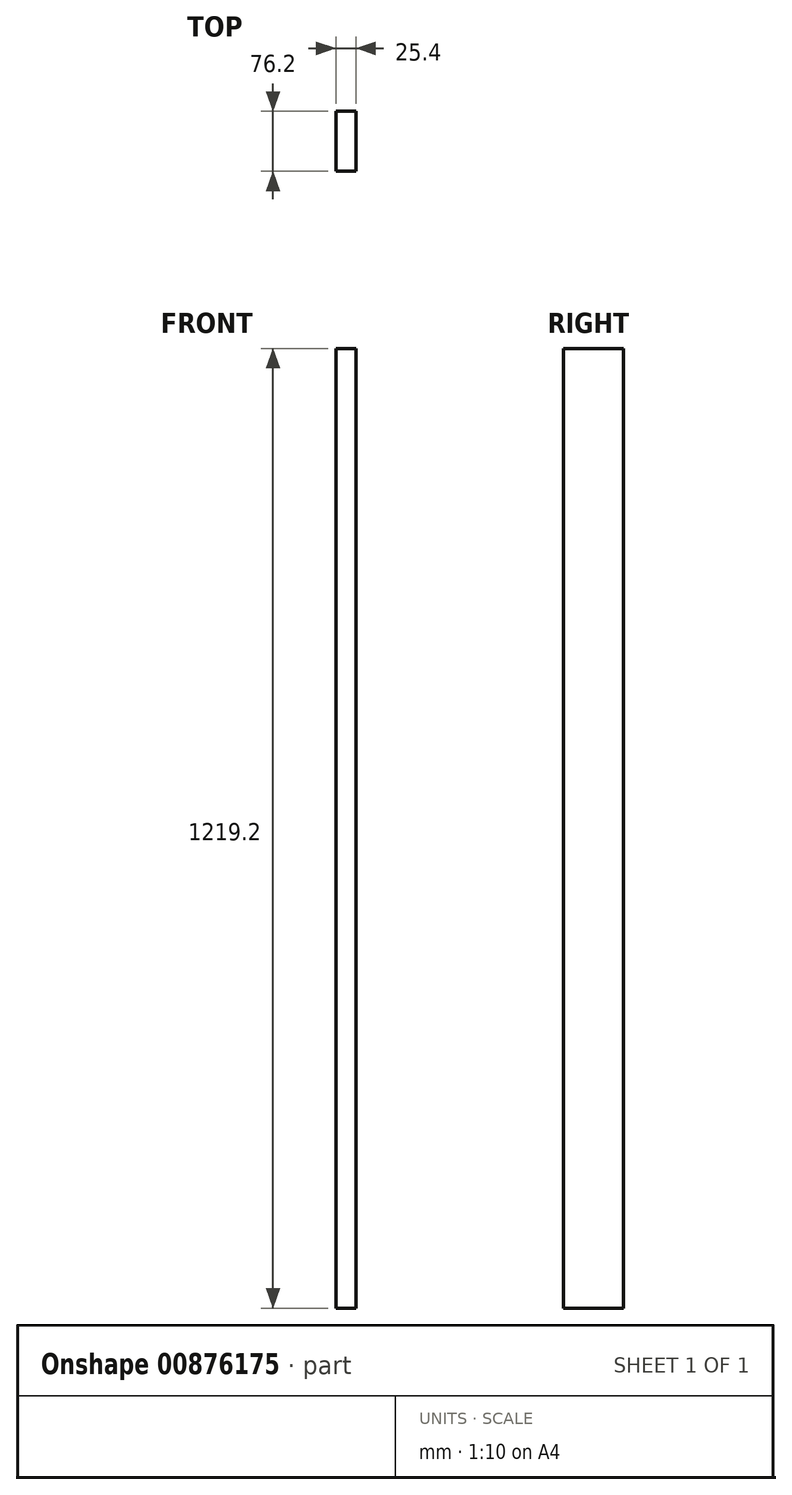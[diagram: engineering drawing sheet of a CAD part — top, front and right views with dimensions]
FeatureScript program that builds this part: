
annotation { "Feature Type Name" : "Feature", "Feature Type Description" : "" }
export const myFeature = defineFeature(function(context is Context, id is Id, definition is map)
    precondition{}
    {
        {
            var Q0;
            Q0=qCreatedBy(makeId("Front.planeOp"),FACE);
            var sketch = newSketch(context, id + "F0", { "sketchPlane" : qUnion([Q0])});
            skLineSegment(sketch, "E0.bottom", {"start": v(-32.22, 1173.32) * mm, "end": v(-57.62, 1173.32) * mm});
            skLineSegment(sketch, "E0.top", {"start": v(-32.22, -45.88) * mm, "end": v(-57.62, -45.88) * mm});
            skLineSegment(sketch, "E0.left", {"start": v(-32.22, 1173.32) * mm, "end": v(-32.22, -45.88) * mm});
            skLineSegment(sketch, "E0.right", {"start": v(-57.62, 1173.32) * mm, "end": v(-57.62, -45.88) * mm});
            skSolve(sketch);
        }
        {
            var Q0;
            Q0=makeQuery(id+"F0.imprint","IMPRINT",FACE,{"disambiguationData":[TD([[makeQuery(id+"F0.imprint","IMPRINT",EDGE,{"derivedFrom":sQuery(id+"F0.wireOp",EDGE,"E0.bottom")}),1.0]])]});
            extrude(context, id + "F1", {"entities" : qUnion([Q0]), "depth" : 76.2 * mm, "offsetDistance" : 25.4 * mm});
        }
    });
